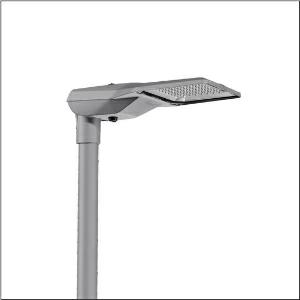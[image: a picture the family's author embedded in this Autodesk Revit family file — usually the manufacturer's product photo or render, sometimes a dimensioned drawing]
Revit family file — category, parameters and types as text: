
# Revit family: streetlight_sl_21_iq_midi___stw1_0a_5xe3e31y08nb_e460
name_source: partatom
category: Lighting Fixtures
units: mm (PartAtom-declared; Revit-internal decimal feet)

## family parameters
Cut with Voids When Loaded = No
Host = Face
Light Source = No
Part Type = Normal
Room Calculation Point = No
Round Connector Dimension = Use Diameter
Shared = No

## types (1)
- --- (1 x LED, 21550 lm, 136.6 W, 3000K)
    Apparent Load = 137 VA
    CIE Flux Codes = 39 75 98 100 100
    Color Rendering = 70
    Color Temperature = 3000K
    Default Elevation = 1800 mm
    Description = Streetlight SL 21 iQ midi, mast luminaire, primary light control with lens, of PMMA, primary optical cover: cover, of toughened safety glass, transparent, light distribution: STW1.0a, light emission: direct distribution, primary light characteristic: asymmetric, installation type: post-top, side-entry, LED, High Power LED, rated luminous flux: 21.550lm, luminous efficacy: 158lm/W, light colour: 730, colour temperature: 3000K, control: pre-setting: logarithmic dimming characteristic, Street-Remote, Auto-Match, Temp-Guard, Lumen-Switch, Night-Set, Smart-Wire, Light-Fading, Desk-Remote (wireless, voltage-free reading and setting of iQ features in the workshop via application-optimized NFC function/RFID function), optimised constant luminous flux control (CLO 2.0), mains connection: 230..240V, AC, 50/60Hz, start of lifetime: 137W, end of service life: 144W, reduction: 61W, luminaire housing, of diecast aluminium, powder-coated, Siteco® metallic grey (DB 702S), corrosivity category C5 mid according to DIN EN ISO 12944, please order mast flange separately, inclination adjustable: 0°, 5°, 10°, 15°, sealing non-destructively replaceable, multi-level sealing system, length: 644mm, width: 335mm, height: 110mm, mast flange for spigot size: 42mm (side-entry): 5XC10008XM4, 60/48mm (side-entry/post-top): 5XC10108XM2, 76/60mm (side-entry/post-top): 5XC10108XM1, Smart Interface below and above, protection rating (complete): IP66, insulation class (complete): insulation class II (safety insulation), certification: CE, ENEC, ENEC+, VDE, impact resistance: IK09, permissible operating ambient temperature for outdoor applications: -40..+50°C, standard-compliant lighting for roads and squares, packaging unit: 1 piece

Light Distribution: STW1.0a
    Height = 111 mm
    Lamp = 1 x LED
    Lamp Light Flux = 21550 lm
    Lamp Power = 136.6 W
    Lamp count = 1
    Length = 644 mm
    Luminous efficacy = 158 lm/W
    Manufacturer = Siteco
    ModVariant = No
    Model = 5XE3E31Y08NB
    Number of Poles = 1
    OnlyDefault = Yes
    Power Factor = 1
    Product Name = Streetlight SL 21 iQ midi | STW1.0a
    Product group = mast luminaire | pylon top
    ProductGroupID = 6100
    Protection Class = Protection class II
    Protection Degree = IP 66
    RLX_Detail_Level = 1
    RLX_Emergency_Light_Flux = 0 lm
    RLX_Emergency_Type = 0
    RLX_Emergency_Type_DB = No
    RlxData = <blob elided: 90909 chars, md5=20b95644>
    Socket = socket
    Standby Power = 0 W
    System Light Flux = 21550 lm
    System Power = 137 W
    Type Comments = factory setting: luminous flux: 100 % | dim-lin: 254 | 733 mA
    Type Image = l_1004304.jpg
    URL = http://relux.com
    VarID = @adj_082501
    Voltage = 0 V
    Weight = 0.00 kg
    Width = 336 mm

## geometry (parser evidence)
native form markers: Blend x4, Sweep x12
no freeform markers — native parametric forms only
